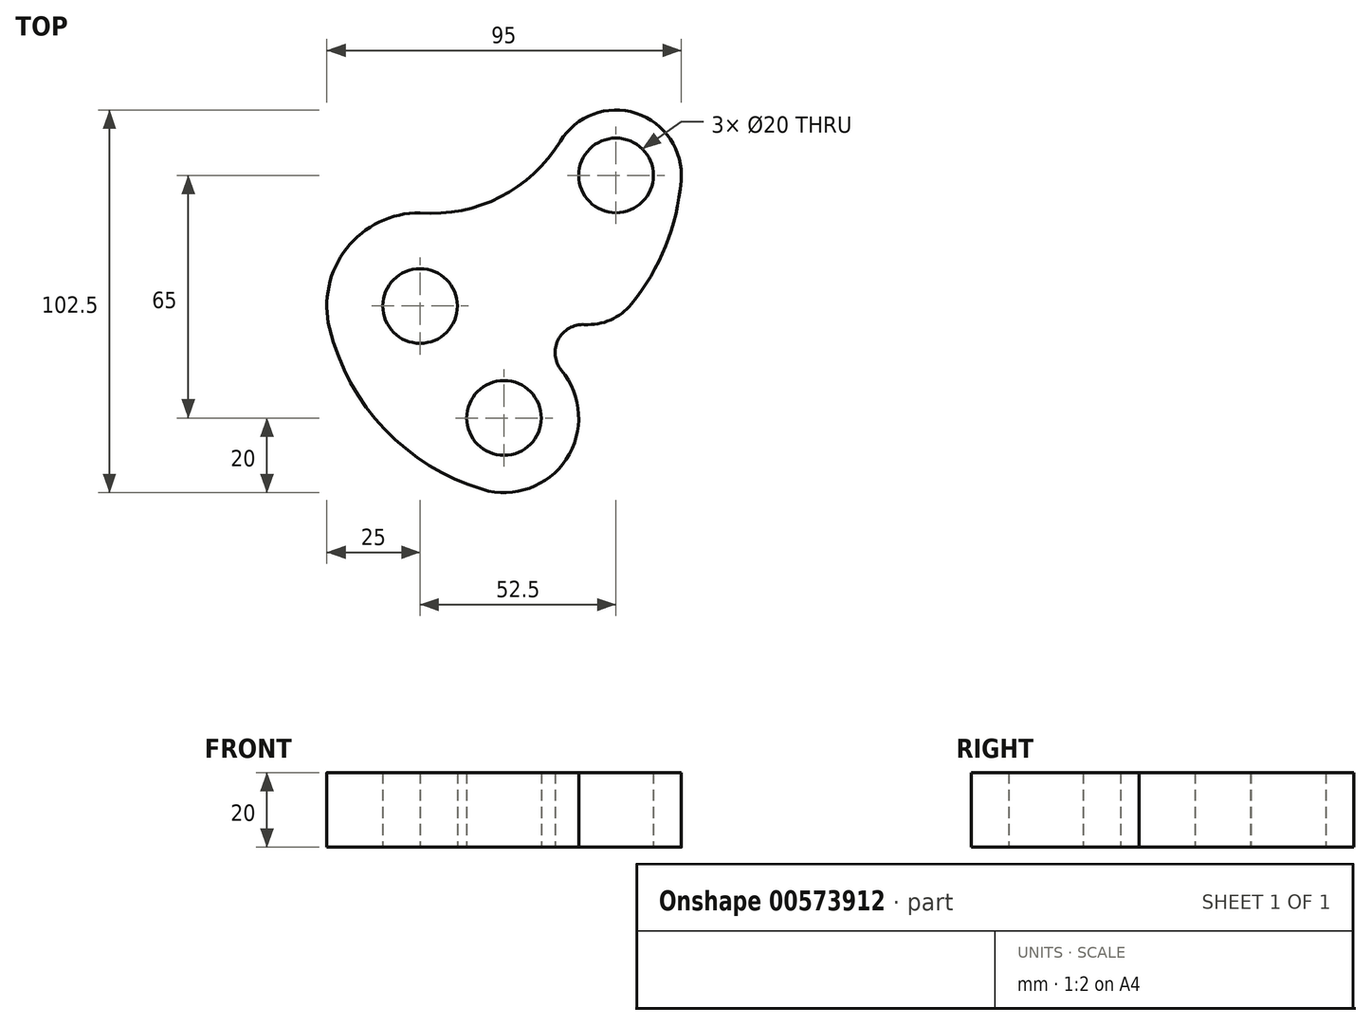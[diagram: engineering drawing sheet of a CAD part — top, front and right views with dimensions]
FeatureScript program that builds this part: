
annotation { "Feature Type Name" : "Feature", "Feature Type Description" : "" }
export const myFeature = defineFeature(function(context is Context, id is Id, definition is map)
    precondition{}
    {
        {
            var Q0;
            Q0=qCreatedBy(makeId("Top.planeOp"),FACE);
            var sketch = newSketch(context, id + "F0", { "sketchPlane" : qUnion([Q0])});
            skArc(sketch, "E0", {"start": v(0, 25) * mm, "mid": v(-19.66, 15.44) * mm, "end": v(-24.28, -5.94) * mm});
            skCircle(sketch, "E1", {"center": v(0, 0) * mm, "radius": 10 * mm});
            skArc(sketch, "E2", {"start": v(69.94, 33.58) * mm, "mid": v(57.9, 51.65) * mm, "end": v(37.54, 44.09) * mm});
            skCircle(sketch, "E3", {"center": v(52.5, 35) * mm, "radius": 10 * mm});
            skArc(sketch, "E4", {"start": v(16.75, -49.16) * mm, "mid": v(39.17, -41.05) * mm, "end": v(37.9, -17.24) * mm});
            skCircle(sketch, "E5", {"center": v(22.5, -30) * mm, "radius": 10 * mm});
            skArc(sketch, "E6", {"start": v(-24.28, -5.94) * mm, "mid": v(-9.51, -33) * mm, "end": v(16.75, -49.16) * mm});
            skArc(sketch, "E7", {"start": v(0, 25) * mm, "mid": v(21.49, 29.2) * mm, "end": v(37.54, 44.09) * mm});
            skArc(sketch, "E8", {"start": v(44.12, -4.97) * mm, "mid": v(37, -9.07) * mm, "end": v(37.9, -17.24) * mm});
            skArc(sketch, "E9", {"start": v(44.12, -4.97) * mm, "mid": v(51.03, -3.73) * mm, "end": v(56.62, 0.51) * mm});
            skArc(sketch, "E10", {"start": v(56.62, 0.51) * mm, "mid": v(65.8, 16.03) * mm, "end": v(69.94, 33.58) * mm});
            skSolve(sketch);
        }
        {
            var Q0;
            Q0=makeQuery(id+"F0.imprint","IMPRINT",FACE,{"disambiguationData":[TD([[makeQuery(id+"F0.imprint","IMPRINT",EDGE,{"derivedFrom":sQuery(id+"F0.wireOp",EDGE,"E0")}),1.0]])]});
            extrude(context, id + "F1", {"entities" : qUnion([Q0]), "depth" : 20 * mm, "offsetDistance" : 25 * mm});
        }
    });
